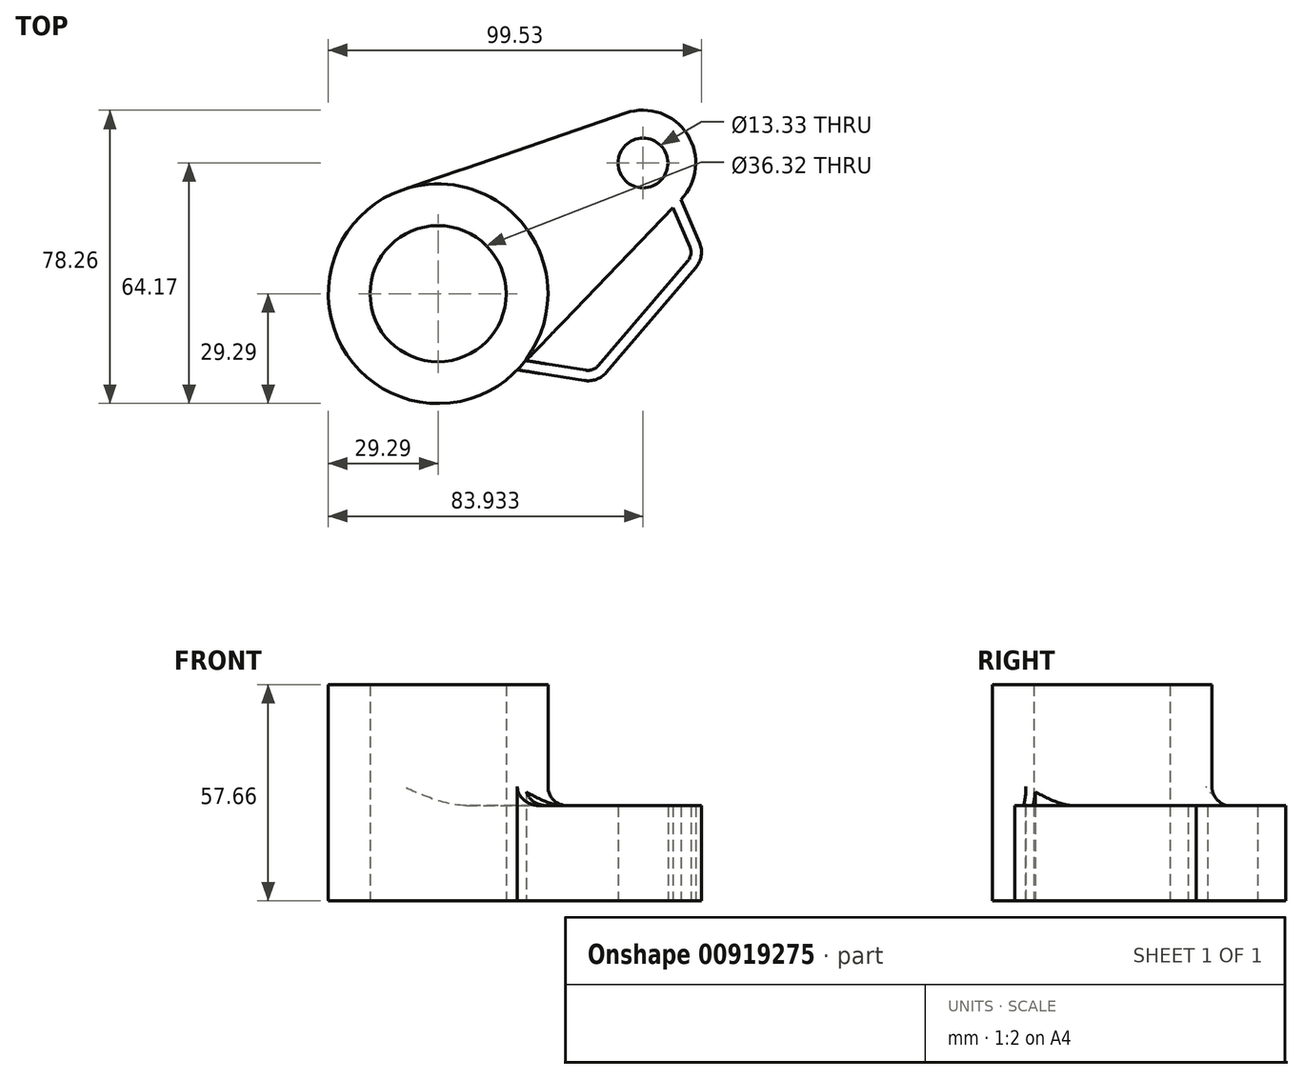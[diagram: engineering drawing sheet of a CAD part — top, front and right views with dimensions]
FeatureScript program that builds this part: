
annotation { "Feature Type Name" : "Feature", "Feature Type Description" : "" }
export const myFeature = defineFeature(function(context is Context, id is Id, definition is map)
    precondition{}
    {
        {
            var Q0;
            Q0=qCreatedBy(makeId("Top.planeOp"),FACE);
            var sketch = newSketch(context, id + "F0", { "sketchPlane" : qUnion([Q0])});
            skCircle(sketch, "E0", {"center": v(0, 0) * mm, "radius": 29.3 * mm});
            skCircle(sketch, "E1", {"center": v(54.64, 34.88) * mm, "radius": 14.09 * mm});
            skLineSegment(sketch, "E2", {"start": v(-9.53, 27.7) * mm, "end": v(50.06, 48.2) * mm});
            skLineSegment(sketch, "E3", {"start": v(21.11, -20.3) * mm, "end": v(64.8, 25.12) * mm});
            skCircle(sketch, "E4", {"center": v(0, 0) * mm, "radius": 18.16 * mm});
            skCircle(sketch, "E5", {"center": v(54.64, 34.88) * mm, "radius": 6.67 * mm});
            skLineSegment(sketch, "E6", {"start": v(21.11, -20.3) * mm, "end": v(38.99, -23.16) * mm});
            skLineSegment(sketch, "E7", {"start": v(44.82, -21.02) * mm, "end": v(68.72, 6.94) * mm});
            skLineSegment(sketch, "E8", {"start": v(69.73, 13.56) * mm, "end": v(64.8, 25.12) * mm});
            skPoint(sketch, "E9.visualSharp", {"position": v(42.5, -23.72) * mm});
            skArc(sketch, "E9.filletArc", {"start": v(38.99, -23.16) * mm, "mid": v(42.18, -22.85) * mm, "end": v(44.82, -21.02) * mm});
            skPoint(sketch, "E10.visualSharp", {"position": v(71.28, 9.94) * mm});
            skArc(sketch, "E10.filletArc", {"start": v(68.72, 6.94) * mm, "mid": v(70.17, 10.1) * mm, "end": v(69.73, 13.56) * mm});
            skLineSegment(sketch, "E11.0", {"start": v(67.16, 12.46) * mm, "end": v(62.7, 22.93) * mm});
            skLineSegment(sketch, "E11.1", {"start": v(23.47, -17.85) * mm, "end": v(39.43, -20.4) * mm});
            skArc(sketch, "E11.2", {"start": v(39.43, -20.4) * mm, "mid": v(41.22, -20.23) * mm, "end": v(42.7, -19.2) * mm});
            skLineSegment(sketch, "E11.3", {"start": v(42.7, -19.2) * mm, "end": v(66.6, 8.76) * mm});
            skArc(sketch, "E11.4", {"start": v(66.6, 8.76) * mm, "mid": v(67.4, 10.53) * mm, "end": v(67.16, 12.46) * mm});
            skSolve(sketch);
        }
        {
            var Q0;
            Q0=makeQuery(id+"F0.imprint","IMPRINT",FACE,{"disambiguationData":[TD([[makeQuery(id+"F0.imprint","IMPRINT",EDGE,{"derivedFrom":sQuery(id+"F0.wireOp",EDGE,"E4")}),-1.0]])]});
            var Q1;
            Q1=makeQuery(id+"F0.imprint","IMPRINT",FACE,{"disambiguationData":[TD([[makeQuery(id+"F0.imprint","IMPRINT",EDGE,{"derivedFrom":sQuery(id+"F0.wireOp",EDGE,"E5")}),-1.0]])]});
            var Q2;
            {var subQ4=sQuery(id+"F0.wireOp",EDGE,"E2");Q2=makeQuery(id+"F0.imprint","IMPRINT",FACE,{"disambiguationData":[TD([[makeQuery(id+"F0.imprint","IMPRINT",EDGE,{"derivedFrom":subQ4}),-1.0]])]});}
            var Q3;
            {var subQ3=sQuery(id+"F0.wireOp",EDGE,"E6");Q3=makeQuery(id+"F0.imprint","IMPRINT",FACE,{"disambiguationData":[TD([[makeQuery(id+"F0.imprint","IMPRINT",EDGE,{"derivedFrom":subQ3}),1.0]])]});}
            extrude(context, id + "F1", {"entities" : qUnion([Q0, Q1, Q2, Q3]), "depth" : 25.4 * mm, "offsetDistance" : 25.4 * mm});
        }
        {
            var Q0;
            Q0=makeQuery(id+"F0.imprint","IMPRINT",FACE,{"disambiguationData":[TD([[makeQuery(id+"F0.imprint","IMPRINT",EDGE,{"derivedFrom":sQuery(id+"F0.wireOp",EDGE,"E4")}),-1.0]])]});
            extrude(context, id + "F2", {"entities" : qUnion([Q0]), "operationType" : NewBodyOperationType.ADD, "depth" : 57.66 * mm, "offsetDistance" : 25.4 * mm});
        }
        {
            var Q0;
            {var subQ0=sQuery(id+"F0.wireOp",EDGE,"E0");Q0=makeQuery(id+"F2.boolean.opBoolean","INTERSECT",EDGE,{"derivedFrom":[makeQuery(id+"F1.opExtrude","CAP_FACE",FACE,{"disambiguationData":[OSD([subQ0,sQuery(id+"F0.wireOp",EDGE,"E1"),sQuery(id+"F0.wireOp",EDGE,"E2"),sQuery(id+"F0.wireOp",EDGE,"E3"),sQuery(id+"F0.wireOp",EDGE,"E4"),sQuery(id+"F0.wireOp",EDGE,"E5"),sQuery(id+"F0.wireOp",EDGE,"E6"),sQuery(id+"F0.wireOp",EDGE,"E7"),sQuery(id+"F0.wireOp",EDGE,"E8"),sQuery(id+"F0.wireOp",EDGE,"E9.filletArc"),sQuery(id+"F0.wireOp",EDGE,"E10.filletArc"),sQuery(id+"F0.wireOp",EDGE,"E11.0"),sQuery(id+"F0.wireOp",EDGE,"E11.1"),sQuery(id+"F0.wireOp",EDGE,"E11.2"),sQuery(id+"F0.wireOp",EDGE,"E11.3"),sQuery(id+"F0.wireOp",EDGE,"E11.4")])],"isStart":false}),makeQuery(id+"F2.opExtrude","SWEPT_FACE",FACE,{"disambiguationData":[OSD([subQ0])]})]});}
            fillet(context, id + "F3", {"entities" : qUnion([Q0]), "radius" : 5.08 * mm, "tangentPropagation" : true, "allowEdgeOverflow" : false});
        }
    });
